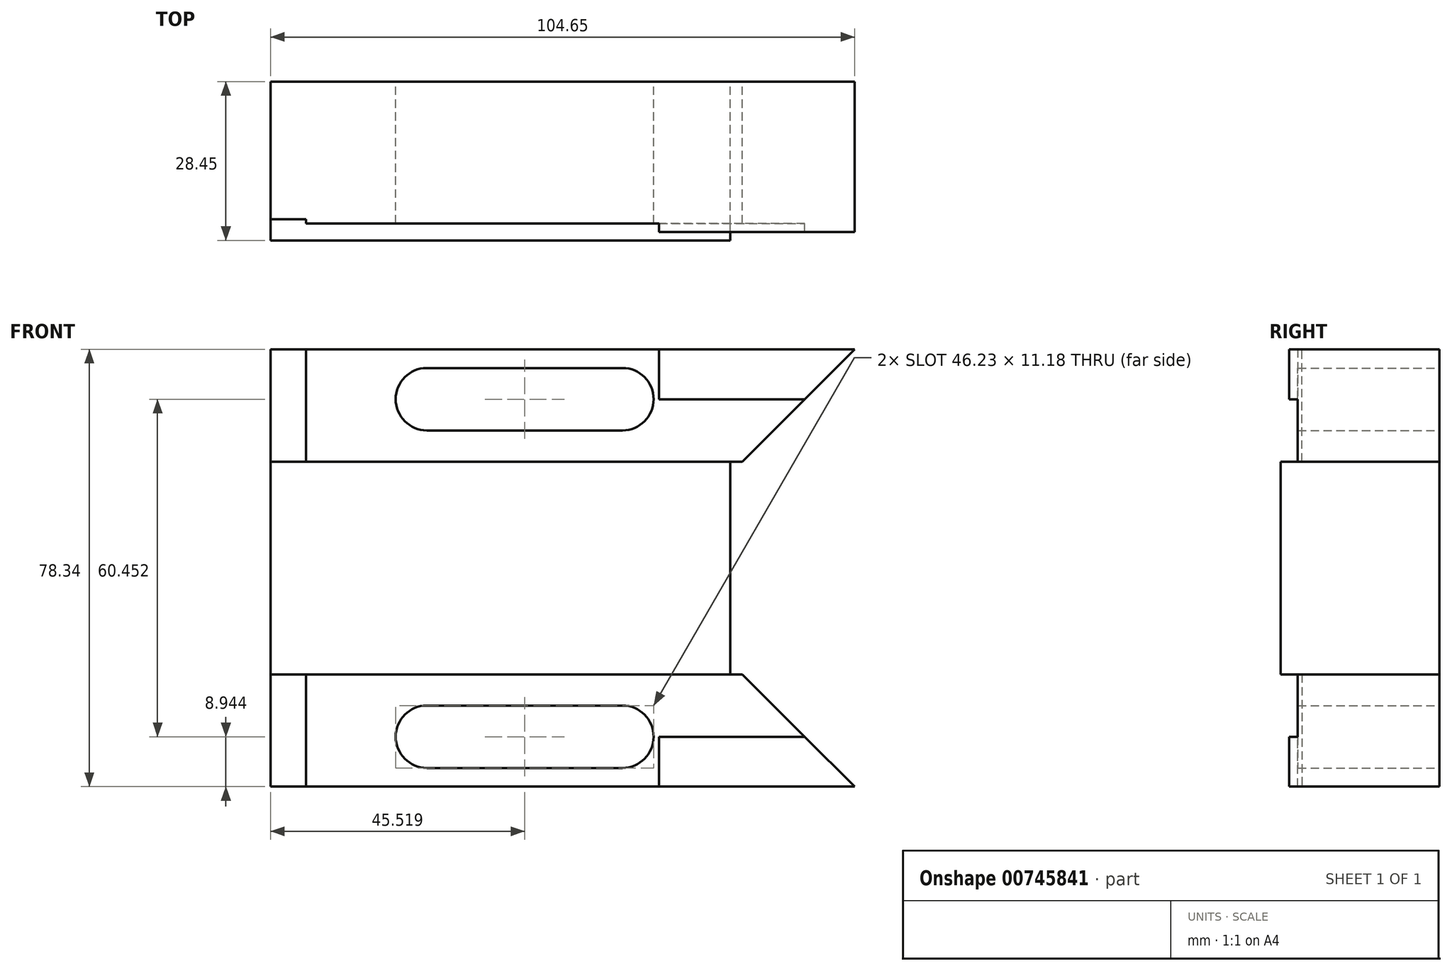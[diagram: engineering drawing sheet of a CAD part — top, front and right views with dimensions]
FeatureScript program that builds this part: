
annotation { "Feature Type Name" : "Feature", "Feature Type Description" : "" }
export const myFeature = defineFeature(function(context is Context, id is Id, definition is map)
    precondition{}
    {
        {
            var Q0;
            Q0=qCreatedBy(makeId("Front.planeOp"),FACE);
            var sketch = newSketch(context, id + "F0", { "sketchPlane" : qUnion([Q0])});
            skLineSegment(sketch, "E0", {"start": v(0, -39.17) * mm, "end": v(104.65, -39.17) * mm});
            skLineSegment(sketch, "E1", {"start": v(104.65, -39.17) * mm, "end": v(84.53, -19.05) * mm});
            skLineSegment(sketch, "E2", {"start": v(84.53, -19.05) * mm, "end": v(0, -19.05) * mm});
            skPoint(sketch, "E3", {"position": v(0, 0) * mm});
            skLineSegment(sketch, "E4", {"start": v(0, 0) * mm, "end": v(0, -39.17) * mm});
            skPoint(sketch, "E5.startSnap0", {"position": v(42.27, -19.05) * mm});
            skLineSegment(sketch, "E6", {"start": v(0, -25.78) * mm, "end": v(6.35, -25.78) * mm, "construction": true});
            skLineSegment(sketch, "E7", {"start": v(6.35, -19.05) * mm, "end": v(6.35, -39.17) * mm});
            skLineSegment(sketch, "E8", {"start": v(0, -34.05) * mm, "end": v(24.64, -34.05) * mm, "construction": true});
            skLineSegment(sketch, "E9", {"start": v(28, -24.64) * mm, "end": v(63.05, -24.64) * mm});
            skArc(sketch, "E10", {"start": v(28, -24.64) * mm, "mid": v(22.4, -30.23) * mm, "end": v(28, -35.81) * mm});
            skLineSegment(sketch, "E11", {"start": v(28, -35.81) * mm, "end": v(63.05, -35.81) * mm});
            skArc(sketch, "E12", {"start": v(63.05, -35.81) * mm, "mid": v(68.63, -30.23) * mm, "end": v(63.05, -24.64) * mm});
            skLineSegment(sketch, "E13.MirrorCS", {"start": v(6.35, 19.05) * mm, "end": v(6.35, 39.17) * mm});
            skLineSegment(sketch, "E14.MirrorCS", {"start": v(84.53, 19.05) * mm, "end": v(0, 19.05) * mm});
            skLineSegment(sketch, "E15.MirrorCS", {"start": v(0, 0) * mm, "end": v(0, 39.17) * mm});
            skLineSegment(sketch, "E16.MirrorCS", {"start": v(104.65, 39.17) * mm, "end": v(84.53, 19.05) * mm});
            skLineSegment(sketch, "E17.MirrorCS", {"start": v(0, 39.17) * mm, "end": v(104.65, 39.17) * mm});
            skArc(sketch, "E18.MirrorCS", {"start": v(63.05, 35.81) * mm, "mid": v(68.63, 30.23) * mm, "end": v(63.05, 24.64) * mm});
            skLineSegment(sketch, "E19.MirrorCS", {"start": v(28, 24.64) * mm, "end": v(63.05, 24.64) * mm});
            skLineSegment(sketch, "E20.MirrorCS", {"start": v(28, 35.81) * mm, "end": v(63.05, 35.81) * mm});
            skArc(sketch, "E21.MirrorCS", {"start": v(28, 24.64) * mm, "mid": v(22.4, 30.23) * mm, "end": v(28, 35.81) * mm});
            skPoint(sketch, "E22.MirrorCS.start.orphan", {"position": v(84.53, 19.05) * mm});
            skLineSegment(sketch, "E23", {"start": v(82.36, 19.05) * mm, "end": v(82.36, -19.05) * mm});
            skLineSegment(sketch, "E24", {"start": v(0, 39.17) * mm, "end": v(0, 59.45) * mm, "construction": true});
            skLineSegment(sketch, "E25", {"start": v(0, 59.45) * mm, "end": v(69.6, 59.45) * mm, "construction": true});
            skLineSegment(sketch, "E26", {"start": v(69.6, 59.45) * mm, "end": v(69.6, 39.17) * mm, "construction": true});
            skLineSegment(sketch, "E27", {"start": v(69.6, 39.17) * mm, "end": v(69.6, 30.23) * mm});
            skPoint(sketch, "E27.endSnap0", {"position": v(68.63, 30.23) * mm});
            skLineSegment(sketch, "E28", {"start": v(69.6, 30.23) * mm, "end": v(95.7, 30.23) * mm});
            skLineSegment(sketch, "E29.MirrorCS", {"start": v(69.6, -30.23) * mm, "end": v(95.7, -30.23) * mm});
            skLineSegment(sketch, "E30.MirrorCS", {"start": v(69.6, -39.17) * mm, "end": v(69.6, -30.23) * mm});
            skSolve(sketch);
        }
        {
            var Q0;
            {var subQ7=sQuery(id+"F0.wireOp",EDGE,"E23");Q0=makeQuery(id+"F0.imprint","IMPRINT",FACE,{"disambiguationData":[TD([[makeQuery(id+"F0.imprint","IMPRINT",EDGE,{"derivedFrom":subQ7}),-1.0]])]});}
            extrude(context, id + "F1", {"entities" : qUnion([Q0]), "depth" : 28.45 * mm, "offsetDistance" : 25.4 * mm});
        }
        {
            var Q0;
            {var subQ2=sQuery(id+"F0.wireOp",EDGE,"E13.MirrorCS");Q0=makeQuery(id+"F0.imprint","IMPRINT",FACE,{"disambiguationData":[TD([[makeQuery(id+"F0.imprint","IMPRINT",EDGE,{"derivedFrom":subQ2}),-1.0]])]});}
            var Q1;
            {var subQ1=sQuery(id+"F0.wireOp",EDGE,"E7");Q1=makeQuery(id+"F0.imprint","IMPRINT",FACE,{"disambiguationData":[TD([[makeQuery(id+"F0.imprint","IMPRINT",EDGE,{"derivedFrom":subQ1}),1.0]])]});}
            extrude(context, id + "F2", {"entities" : qUnion([Q0, Q1]), "operationType" : NewBodyOperationType.ADD, "depth" : 25.4 * mm, "offsetDistance" : 25.4 * mm});
        }
        {
            var Q0;
            {var subQ4=sQuery(id+"F0.wireOp",EDGE,"E29.MirrorCS");Q0=makeQuery(id+"F0.imprint","IMPRINT",FACE,{"disambiguationData":[TD([[makeQuery(id+"F0.imprint","IMPRINT",EDGE,{"derivedFrom":subQ4}),-1.0]])]});}
            extrude(context, id + "F3", {"entities" : qUnion([Q0]), "operationType" : NewBodyOperationType.ADD, "depth" : 26.92 * mm, "offsetDistance" : 25.4 * mm});
        }
        {
            var Q0;
            {var subQ4=sQuery(id+"F0.wireOp",EDGE,"E27");Q0=makeQuery(id+"F0.imprint","IMPRINT",FACE,{"disambiguationData":[TD([[makeQuery(id+"F0.imprint","IMPRINT",EDGE,{"derivedFrom":subQ4}),1.0]])]});}
            extrude(context, id + "F4", {"entities" : qUnion([Q0]), "operationType" : NewBodyOperationType.ADD, "depth" : 26.92 * mm, "offsetDistance" : 25.4 * mm});
        }
        {
            var Q0;
            {var subQ3=sQuery(id+"F0.wireOp",EDGE,"E7");Q0=makeQuery(id+"F0.imprint","IMPRINT",FACE,{"disambiguationData":[TD([[makeQuery(id+"F0.imprint","IMPRINT",EDGE,{"derivedFrom":subQ3}),-1.0]])]});}
            var Q1;
            {var subQ0=sQuery(id+"F0.wireOp",EDGE,"E13.MirrorCS");Q1=makeQuery(id+"F0.imprint","IMPRINT",FACE,{"disambiguationData":[TD([[makeQuery(id+"F0.imprint","IMPRINT",EDGE,{"derivedFrom":subQ0}),1.0]])]});}
            extrude(context, id + "F5", {"entities" : qUnion([Q0, Q1]), "operationType" : NewBodyOperationType.ADD, "depth" : 24.64 * mm, "offsetDistance" : 25.4 * mm});
        }
    });
